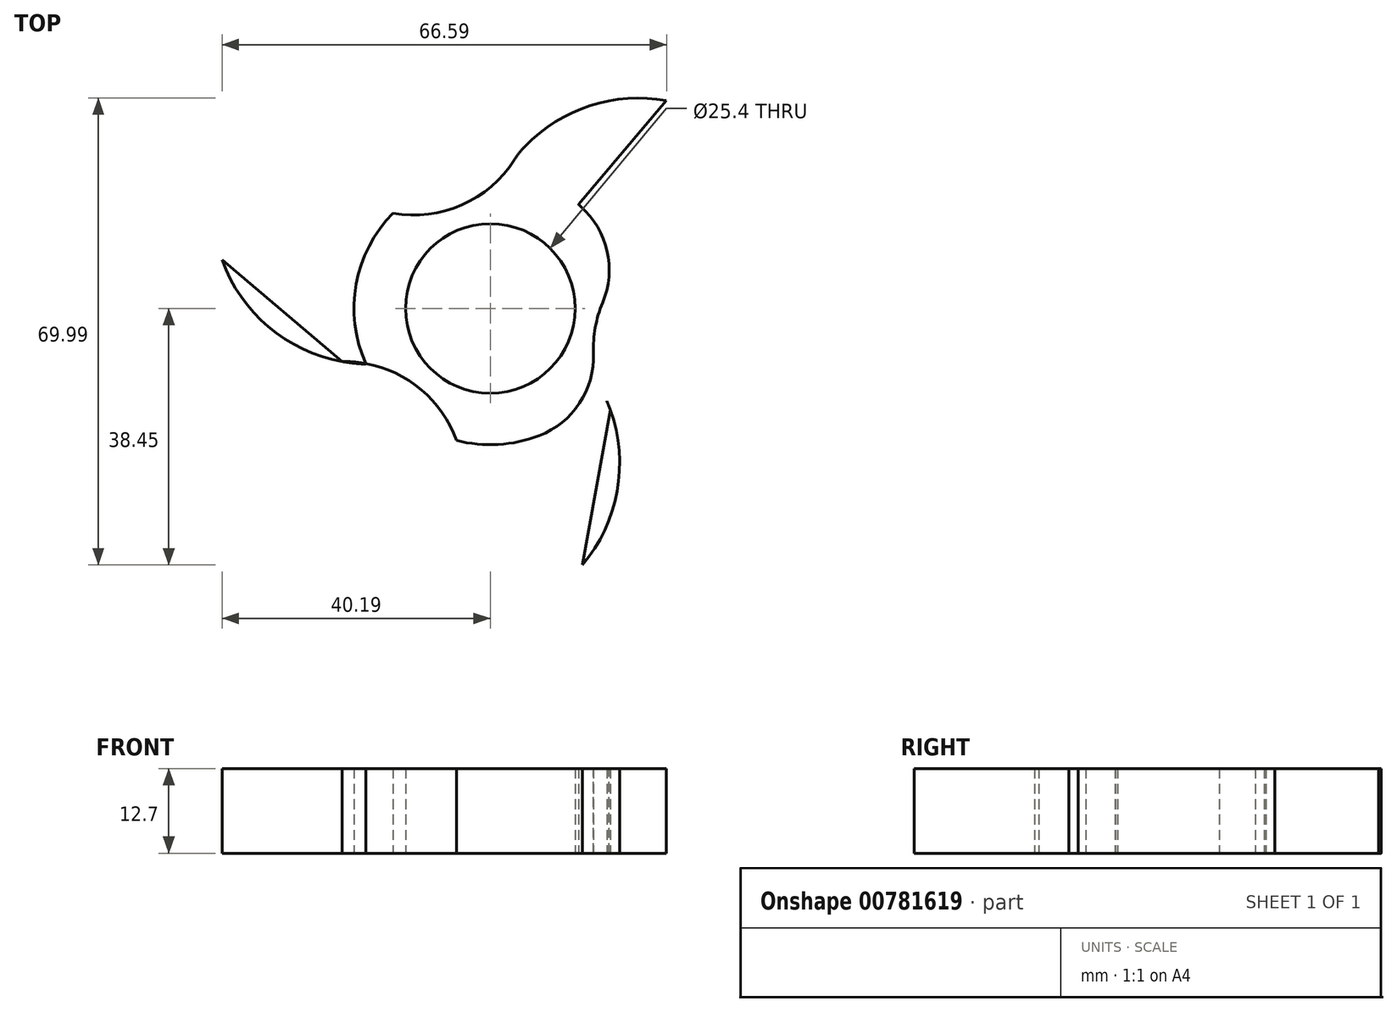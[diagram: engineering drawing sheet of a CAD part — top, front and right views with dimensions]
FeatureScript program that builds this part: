
annotation { "Feature Type Name" : "Feature", "Feature Type Description" : "" }
export const myFeature = defineFeature(function(context is Context, id is Id, definition is map)
    precondition{}
    {
        {
            var Q0;
            Q0=qCreatedBy(makeId("Top.planeOp"),FACE);
            var sketch = newSketch(context, id + "F0", { "sketchPlane" : qUnion([Q0])});
            skPoint(sketch, "E0.end.orphan", {"position": v(3.61, 6.87) * mm});
            skPoint(sketch, "E1.start.orphan", {"position": v(21.36, 37.3) * mm});
            skPoint(sketch, "E2.end.orphan", {"position": v(-3.61, 6.87) * mm});
            skPoint(sketch, "E3.center.orphan", {"position": v(6.07, 37.3) * mm});
            skCircle(sketch, "E4.cCircle", {"center": v(0, 0) * mm, "radius": 20.42 * mm, "construction": true});
            skLineSegment(sketch, "E4.0", {"start": v(26.4, 31.17) * mm, "end": v(13.8, -38.45) * mm});
            skLineSegment(sketch, "E4.1", {"start": v(13.8, -38.45) * mm, "end": v(-40.2, 7.28) * mm});
            skLineSegment(sketch, "E4.2", {"start": v(-40.2, 7.28) * mm, "end": v(26.4, 31.17) * mm});
            skPoint(sketch, "E4.0.midPoint", {"position": v(20.1, -3.64) * mm});
            skCircle(sketch, "E5", {"center": v(0, 0) * mm, "radius": 12.7 * mm});
            skLineSegment(sketch, "E6", {"start": v(-40.2, 7.28) * mm, "end": v(0, 0) * mm});
            skLineSegment(sketch, "E7", {"start": v(26.4, 31.17) * mm, "end": v(0, 0) * mm});
            skLineSegment(sketch, "E8", {"start": v(13.8, -38.45) * mm, "end": v(0, 0) * mm});
            skArc(sketch, "E9", {"start": v(-40.2, 7.28) * mm, "mid": v(-22.2, -7.96) * mm, "end": v(0, 0) * mm});
            skArc(sketch, "E10", {"start": v(13.8, -38.45) * mm, "mid": v(18, -15.24) * mm, "end": v(0, 0) * mm});
            skArc(sketch, "E11", {"start": v(26.4, 31.17) * mm, "mid": v(4.2, 23.2) * mm, "end": v(0, 0) * mm});
            skCircle(sketch, "E12", {"center": v(0, 0) * mm, "radius": 20.42 * mm});
            skLineSegment(sketch, "E13", {"start": v(-20.1, 3.64) * mm, "end": v(-40.2, 7.28) * mm});
            skLineSegment(sketch, "E14", {"start": v(26.4, 31.17) * mm, "end": v(13.2, 15.58) * mm});
            skLineSegment(sketch, "E15", {"start": v(6.9, -19.22) * mm, "end": v(13.8, -38.45) * mm});
            skPoint(sketch, "E16.center.orphan", {"position": v(-30.14, 5.46) * mm});
            skArc(sketch, "E17", {"start": v(0, 0) * mm, "mid": v(-18, 15.24) * mm, "end": v(-40.2, 7.28) * mm});
            skArc(sketch, "E18", {"start": v(0, 0) * mm, "mid": v(22.18, 7.97) * mm, "end": v(26.4, 31.17) * mm});
            skArc(sketch, "E19", {"start": v(0, 0) * mm, "mid": v(-3.44, -5.4) * mm, "end": v(-5.3, -11.54) * mm});
            skArc(sketch, "E20.trimOffspring", {"start": v(-5.15, -19.76) * mm, "mid": v(1.43, -32.03) * mm, "end": v(13.8, -38.45) * mm});
            skArc(sketch, "E21", {"start": v(-4.2, -23.2) * mm, "mid": v(-10.33, -12.2) * mm, "end": v(-22.2, -7.96) * mm});
            skArc(sketch, "E22", {"start": v(-18, 15.24) * mm, "mid": v(-5.4, 15.07) * mm, "end": v(4.17, 23.23) * mm});
            skArc(sketch, "E23", {"start": v(22.2, 7.96) * mm, "mid": v(20.93, 6.53) * mm, "end": v(19.8, 5) * mm});
            skArc(sketch, "E24.trimOffspring", {"start": v(16.8, -11.62) * mm, "mid": v(17.31, -13.46) * mm, "end": v(18, -15.24) * mm});
            skArc(sketch, "E25", {"start": v(22.2, 7.96) * mm, "mid": v(15.73, -2.85) * mm, "end": v(18, -15.24) * mm});
            skSolve(sketch);
        }
        {
            var Q0;
            {var subQ2=sQuery(id+"F0.wireOp",EDGE,"E11");var subQ4=sQuery(id+"F0.wireOp",EDGE,"E5");var subQ5=makeQuery(id+"F0.imprint","INTERSECT",VERTEX,{"derivedFrom":[subQ4,subQ2]});Q0=makeQuery(id+"F0.imprint","IMPRINT",FACE,{"disambiguationData":[TD([[makeQuery(id+"F0.imprint","IMPRINT",EDGE,{"disambiguationData":[TD([[subQ5,-1.0]])],"derivedFrom":subQ4}),-1.0]])]});}
            var Q1;
            {var subQ0=sQuery(id+"F0.wireOp",EDGE,"E6");var subQ1=sQuery(id+"F0.wireOp",EDGE,"E5");var subQ2=makeQuery(id+"F0.imprint","INTERSECT",VERTEX,{"derivedFrom":[subQ1,subQ0]});Q1=makeQuery(id+"F0.imprint","IMPRINT",FACE,{"disambiguationData":[TD([[makeQuery(id+"F0.imprint","IMPRINT",EDGE,{"disambiguationData":[TD([[subQ2,-1.0]])],"derivedFrom":subQ1}),-1.0]])]});}
            var Q2;
            {var subQ2=sQuery(id+"F0.wireOp",EDGE,"E9");var subQ4=sQuery(id+"F0.wireOp",EDGE,"E5");var subQ5=makeQuery(id+"F0.imprint","INTERSECT",VERTEX,{"derivedFrom":[subQ4,subQ2]});Q2=makeQuery(id+"F0.imprint","IMPRINT",FACE,{"disambiguationData":[TD([[makeQuery(id+"F0.imprint","IMPRINT",EDGE,{"disambiguationData":[TD([[subQ5,-1.0]])],"derivedFrom":subQ4}),-1.0]])]});}
            var Q3;
            {var subQ0=sQuery(id+"F0.wireOp",EDGE,"E8");var subQ1=sQuery(id+"F0.wireOp",EDGE,"E5");var subQ2=makeQuery(id+"F0.imprint","INTERSECT",VERTEX,{"derivedFrom":[subQ1,subQ0]});Q3=makeQuery(id+"F0.imprint","IMPRINT",FACE,{"disambiguationData":[TD([[makeQuery(id+"F0.imprint","IMPRINT",EDGE,{"disambiguationData":[TD([[subQ2,-1.0]])],"derivedFrom":subQ1}),-1.0]])]});}
            var Q4;
            {var subQ4=sQuery(id+"F0.wireOp",EDGE,"E5");var subQ6=sQuery(id+"F0.wireOp",EDGE,"E7");var subQ7=makeQuery(id+"F0.imprint","INTERSECT",VERTEX,{"derivedFrom":[subQ4,subQ6]});Q4=makeQuery(id+"F0.imprint","IMPRINT",FACE,{"disambiguationData":[TD([[makeQuery(id+"F0.imprint","IMPRINT",EDGE,{"disambiguationData":[TD([[subQ7,1.0]])],"derivedFrom":subQ4}),-1.0]])]});}
            var Q5;
            {var subQ0=sQuery(id+"F0.wireOp",EDGE,"E11");var subQ1=sQuery(id+"F0.wireOp",EDGE,"E5");var subQ2=makeQuery(id+"F0.imprint","INTERSECT",VERTEX,{"derivedFrom":[subQ1,subQ0]});Q5=makeQuery(id+"F0.imprint","IMPRINT",FACE,{"disambiguationData":[TD([[makeQuery(id+"F0.imprint","IMPRINT",EDGE,{"disambiguationData":[TD([[subQ2,1.0]])],"derivedFrom":subQ1}),-1.0]])]});}
            var Q6;
            {var subQ0=sQuery(id+"F0.wireOp",EDGE,"E9");var subQ2=sQuery(id+"F0.wireOp",EDGE,"E4.1");var subQ4=makeQuery(id+"F0.imprint","INTERSECT",VERTEX,{"derivedFrom":[subQ2,subQ0]});Q6=makeQuery(id+"F0.imprint","IMPRINT",FACE,{"disambiguationData":[TD([[makeQuery(id+"F0.imprint","IMPRINT",EDGE,{"disambiguationData":[TD([[subQ4,-1.0]])],"derivedFrom":subQ0}),1.0]])]});}
            var Q7;
            {var subQ0=sQuery(id+"F0.wireOp",EDGE,"E9");var subQ1=sQuery(id+"F0.wireOp",EDGE,"E4.1");var subQ3=makeQuery(id+"F0.imprint","INTERSECT",VERTEX,{"derivedFrom":[subQ1,subQ0]});Q7=makeQuery(id+"F0.imprint","IMPRINT",FACE,{"disambiguationData":[TD([[makeQuery(id+"F0.imprint","IMPRINT",EDGE,{"disambiguationData":[TD([[subQ3,-1.0]])],"derivedFrom":subQ1}),1.0]])]});}
            var Q8;
            {var subQ0=sQuery(id+"F0.wireOp",EDGE,"E11");var subQ2=sQuery(id+"F0.wireOp",EDGE,"E4.2");var subQ4=makeQuery(id+"F0.imprint","INTERSECT",VERTEX,{"derivedFrom":[subQ2,subQ0]});Q8=makeQuery(id+"F0.imprint","IMPRINT",FACE,{"disambiguationData":[TD([[makeQuery(id+"F0.imprint","IMPRINT",EDGE,{"disambiguationData":[TD([[subQ4,-1.0]])],"derivedFrom":subQ0}),1.0]])]});}
            var Q9;
            {var subQ0=sQuery(id+"F0.wireOp",EDGE,"E11");var subQ1=sQuery(id+"F0.wireOp",EDGE,"E4.2");var subQ3=makeQuery(id+"F0.imprint","INTERSECT",VERTEX,{"derivedFrom":[subQ1,subQ0]});Q9=makeQuery(id+"F0.imprint","IMPRINT",FACE,{"disambiguationData":[TD([[makeQuery(id+"F0.imprint","IMPRINT",EDGE,{"disambiguationData":[TD([[subQ3,-1.0]])],"derivedFrom":subQ1}),1.0]])]});}
            var Q10;
            {var subQ0=sQuery(id+"F0.wireOp",EDGE,"E10");var subQ1=sQuery(id+"F0.wireOp",EDGE,"E4.0");var subQ3=makeQuery(id+"F0.imprint","INTERSECT",VERTEX,{"derivedFrom":[subQ1,subQ0]});Q10=makeQuery(id+"F0.imprint","IMPRINT",FACE,{"disambiguationData":[TD([[makeQuery(id+"F0.imprint","IMPRINT",EDGE,{"disambiguationData":[TD([[subQ3,-1.0]])],"derivedFrom":subQ1}),1.0]])]});}
            var Q11;
            {var subQ0=sQuery(id+"F0.wireOp",EDGE,"E10");var subQ2=sQuery(id+"F0.wireOp",EDGE,"E4.0");var subQ4=makeQuery(id+"F0.imprint","INTERSECT",VERTEX,{"derivedFrom":[subQ2,subQ0]});Q11=makeQuery(id+"F0.imprint","IMPRINT",FACE,{"disambiguationData":[TD([[makeQuery(id+"F0.imprint","IMPRINT",EDGE,{"disambiguationData":[TD([[subQ4,-1.0]])],"derivedFrom":subQ0}),1.0]])]});}
            var Q12;
            {var subQ4=sQuery(id+"F0.wireOp",EDGE,"E5");var subQ6=sQuery(id+"F0.wireOp",EDGE,"E18");var subQ8=makeQuery(id+"F0.imprint","INTERSECT",VERTEX,{"derivedFrom":[subQ4,subQ6]});Q12=makeQuery(id+"F0.imprint","IMPRINT",FACE,{"disambiguationData":[TD([[makeQuery(id+"F0.imprint","IMPRINT",EDGE,{"disambiguationData":[TD([[subQ8,1.0]])],"derivedFrom":subQ4}),-1.0]])]});}
            var Q13;
            {var subQ0=sQuery(id+"F0.wireOp",EDGE,"E17");var subQ1=sQuery(id+"F0.wireOp",EDGE,"E5");var subQ2=makeQuery(id+"F0.imprint","INTERSECT",VERTEX,{"derivedFrom":[subQ1,subQ0]});Q13=makeQuery(id+"F0.imprint","IMPRINT",FACE,{"disambiguationData":[TD([[makeQuery(id+"F0.imprint","IMPRINT",EDGE,{"disambiguationData":[TD([[subQ2,-1.0]])],"derivedFrom":subQ1}),-1.0]])]});}
            var Q14;
            {var subQ0=sQuery(id+"F0.wireOp",EDGE,"E13");Q14=makeQuery(id+"F0.imprint","IMPRINT",FACE,{"disambiguationData":[TD([[makeQuery(id+"F0.imprint","IMPRINT",EDGE,{"derivedFrom":subQ0}),1.0]])]});}
            var Q15;
            {var subQ0=sQuery(id+"F0.wireOp",EDGE,"E15");Q15=makeQuery(id+"F0.imprint","IMPRINT",FACE,{"disambiguationData":[TD([[makeQuery(id+"F0.imprint","IMPRINT",EDGE,{"derivedFrom":subQ0}),1.0]])]});}
            extrude(context, id + "F1", {"entities" : qUnion([Q0, Q1, Q2, Q3, Q4, Q5, Q6, Q7, Q8, Q9, Q10, Q11, Q12, Q13, Q14, Q15]), "depth" : 12.7 * mm, "offsetDistance" : 25 * mm});
        }
        {
            var Q0;
            Q0=makeQuery(id+"F1.opExtrude","SWEPT_EDGE",EDGE,{"disambiguationData":[OSD([sQuery(id+"F0.wireOp",EDGE,"E4.1"),sQuery(id+"F0.wireOp",EDGE,"E20.trimOffspring"),sQuery(id+"F0.wireOp",EDGE,"E21")])]});
            var Q1;
            Q1=makeQuery(id+"F1.opExtrude","SWEPT_EDGE",EDGE,{"disambiguationData":[OSD([sQuery(id+"F0.wireOp",EDGE,"E9"),sQuery(id+"F0.wireOp",EDGE,"E12")])]});
            var Q2;
            Q2=makeQuery(id+"F1.opExtrude","SWEPT_EDGE",EDGE,{"disambiguationData":[OSD([sQuery(id+"F0.wireOp",EDGE,"E4.2"),sQuery(id+"F0.wireOp",EDGE,"E17"),sQuery(id+"F0.wireOp",EDGE,"E22")])]});
            var Q3;
            Q3=makeQuery(id+"F1.opExtrude","SWEPT_EDGE",EDGE,{"disambiguationData":[OSD([sQuery(id+"F0.wireOp",EDGE,"E11"),sQuery(id+"F0.wireOp",EDGE,"E22")])]});
            var Q4;
            Q4=makeQuery(id+"F1.opExtrude","SWEPT_EDGE",EDGE,{"disambiguationData":[OSD([sQuery(id+"F0.wireOp",EDGE,"E18"),sQuery(id+"F0.wireOp",EDGE,"E25")])]});
            var Q5;
            Q5=makeQuery(id+"F1.opExtrude","SWEPT_EDGE",EDGE,{"disambiguationData":[OSD([sQuery(id+"F0.wireOp",EDGE,"E4.0"),sQuery(id+"F0.wireOp",EDGE,"E10"),sQuery(id+"F0.wireOp",EDGE,"E24.trimOffspring"),sQuery(id+"F0.wireOp",EDGE,"E25")]),OD(0.0)]});
            fillet(context, id + "F2", {"entities" : qUnion([Q0, Q1, Q2, Q3, Q4, Q5]), "radius" : 12.7 * mm, "tangentPropagation" : true, "allowEdgeOverflow" : false});
        }
    });
